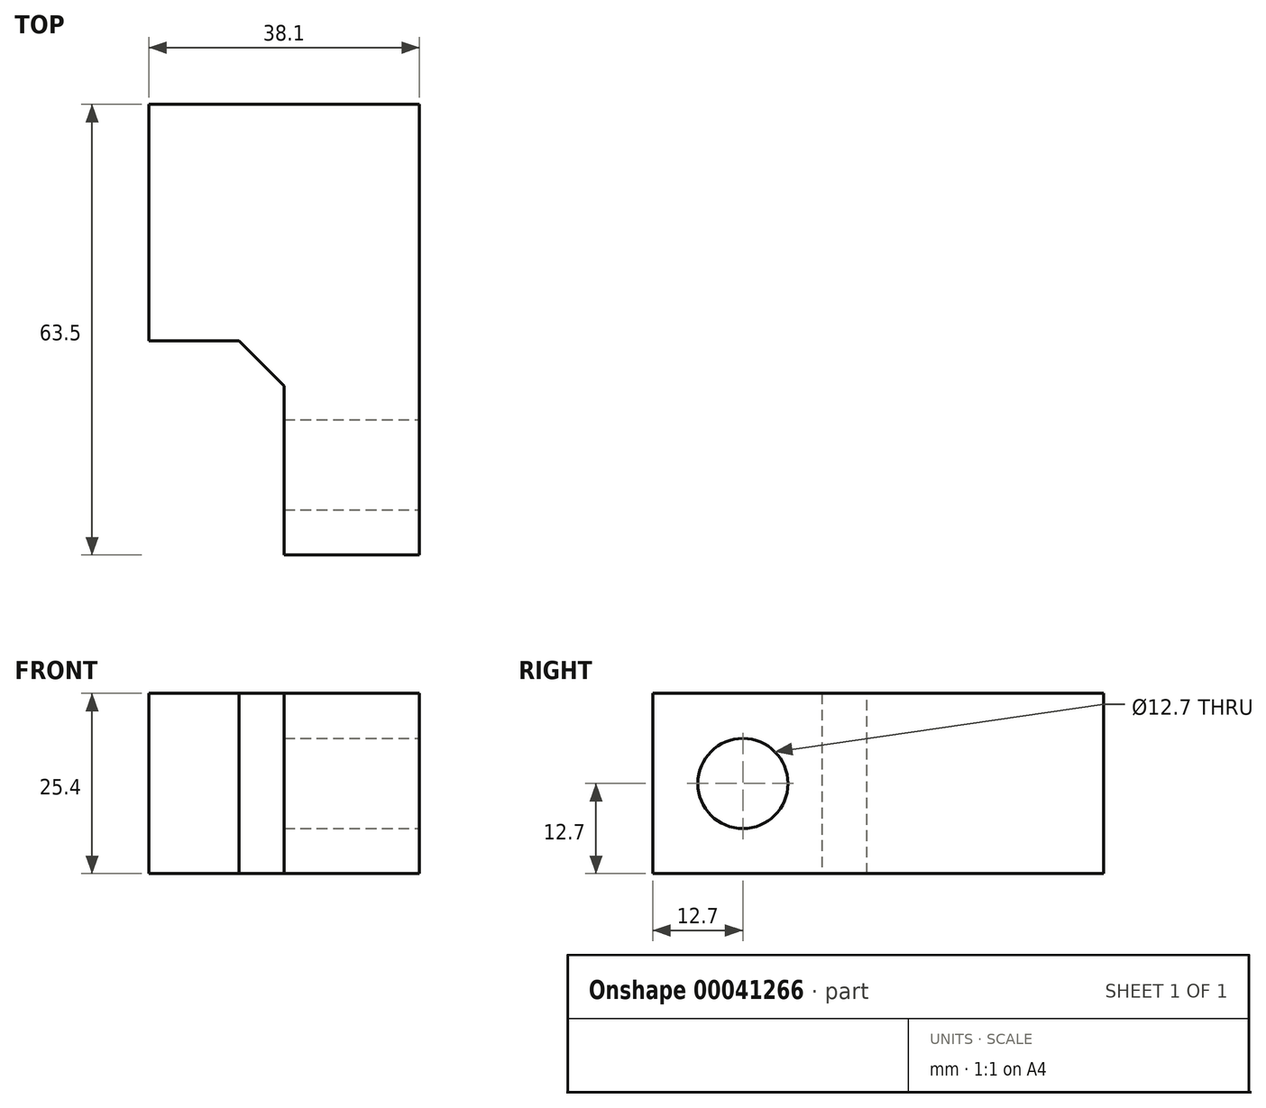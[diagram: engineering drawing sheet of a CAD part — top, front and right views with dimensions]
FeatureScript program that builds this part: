
annotation { "Feature Type Name" : "Feature", "Feature Type Description" : "" }
export const myFeature = defineFeature(function(context is Context, id is Id, definition is map)
    precondition{}
    {
        {
            var Q0;
            Q0=qCreatedBy(makeId("Top.planeOp"),FACE);
            var sketch = newSketch(context, id + "F0", { "sketchPlane" : qUnion([Q0])});
            skLineSegment(sketch, "E0.rect.bottom", {"start": v(-19.05, 31.75) * mm, "end": v(19.05, 31.75) * mm});
            skLineSegment(sketch, "E0.rect.top", {"start": v(-19.05, -31.75) * mm, "end": v(19.05, -31.75) * mm});
            skLineSegment(sketch, "E0.rect.left", {"start": v(-19.05, 31.75) * mm, "end": v(-19.05, -31.75) * mm});
            skLineSegment(sketch, "E0.rect.right", {"start": v(19.05, 31.75) * mm, "end": v(19.05, -31.75) * mm});
            skPoint(sketch, "E0.rect.middle", {"position": v(0, 0) * mm});
            skSolve(sketch);
        }
        {
            var Q0;
            Q0=makeQuery(id+"F0.imprint","IMPRINT",FACE,{"disambiguationData":[TD([[makeQuery(id+"F0.imprint","IMPRINT",EDGE,{"derivedFrom":sQuery(id+"F0.wireOp",EDGE,"E0.rect.bottom")}),-1.0]])]});
            extrude(context, id + "F1", {"entities" : qUnion([Q0]), "depth" : 25.4 * mm});
        }
        {
            var Q0;
            Q0=makeQuery(id+"F1.opExtrude","CAP_FACE",FACE,{"disambiguationData":[OSD([sQuery(id+"F0.wireOp",EDGE,"E0.rect.bottom"),sQuery(id+"F0.wireOp",EDGE,"E0.rect.top"),sQuery(id+"F0.wireOp",EDGE,"E0.rect.left"),sQuery(id+"F0.wireOp",EDGE,"E0.rect.right")])],"isStart":false});
            var sketch = newSketch(context, id + "F2", { "sketchPlane" : qUnion([Q0])});
            skLineSegment(sketch, "E1.bottom", {"start": v(-19.05, -31.75) * mm, "end": v(0, -31.75) * mm});
            skLineSegment(sketch, "E1.top", {"start": v(-19.05, -4.76) * mm, "end": v(0, -4.76) * mm});
            skLineSegment(sketch, "E1.left", {"start": v(-19.05, -31.75) * mm, "end": v(-19.05, -4.76) * mm});
            skLineSegment(sketch, "E1.right", {"start": v(0, -31.75) * mm, "end": v(0, -4.76) * mm});
            skSolve(sketch);
        }
        {
            var Q0;
            Q0=makeQuery(id+"F2.imprint","IMPRINT",FACE,{"disambiguationData":[TD([[makeQuery(id+"F2.imprint","IMPRINT",EDGE,{"derivedFrom":sQuery(id+"F2.wireOp",EDGE,"E1.bottom")}),1.0]])]});
            extrude(context, id + "F3", {"entities" : qUnion([Q0]), "operationType" : NewBodyOperationType.REMOVE, "oppositeDirection" : true, "depth" : 25.4 * mm});
        }
        {
            var Q0;
            Q0=makeQuery(id+"F1.opExtrude","SWEPT_FACE",FACE,{"disambiguationData":[OSD([sQuery(id+"F0.wireOp",EDGE,"E0.rect.right")])]});
            var sketch = newSketch(context, id + "F4", { "sketchPlane" : qUnion([Q0])});
            skCircle(sketch, "E2", {"center": v(-19.05, 12.7) * mm, "radius": 6.35 * mm});
            skSolve(sketch);
        }
        {
            var Q0;
            Q0=makeQuery(id+"F4.imprint","IMPRINT",FACE,{"disambiguationData":[TD([[makeQuery(id+"F4.imprint","IMPRINT",EDGE,{"derivedFrom":sQuery(id+"F4.wireOp",EDGE,"E2")}),1.0]])]});
            extrude(context, id + "F5", {"entities" : qUnion([Q0]), "operationType" : NewBodyOperationType.REMOVE, "oppositeDirection" : true, "depth" : 25.4 * mm});
        }
        {
            var Q0;
            Q0=makeQuery(id+"F3.boolean.opBoolean","COPY",FACE,{"derivedFrom":makeQuery(id+"F3.opExtrude","SWEPT_FACE",FACE,{"disambiguationData":[OSD([sQuery(id+"F2.wireOp",EDGE,"E1.top")])]})});
            extrude(context, id + "F6", {"entities" : qUnion([Q0]), "operationType" : NewBodyOperationType.REMOVE, "oppositeDirection" : true, "depth" : 3.17 * mm});
        }
        {
            var Q0;
            {var subQ0=sQuery(id+"F2.wireOp",EDGE,"E1.top");Q0=makeQuery(id+"F6.boolean.opBoolean","COPY",EDGE,{"derivedFrom":makeQuery(id+"F6.opExtrude","CAP_EDGE",EDGE,{"disambiguationData":[OSD([subQ0]),TDD([makeQuery(id+"F3.boolean.opBoolean","COPY",EDGE,{"derivedFrom":makeQuery(id+"F3.opExtrude","CAP_EDGE",EDGE,{"disambiguationData":[OSD([subQ0])],"isStart":true})})])],"isStart":false})});}
            var Q1;
            {var subQ0=sQuery(id+"F2.wireOp",EDGE,"E1.top");Q1=makeQuery(id+"F6.boolean.opBoolean","COPY",EDGE,{"derivedFrom":makeQuery(id+"F6.opExtrude","CAP_EDGE",EDGE,{"disambiguationData":[OSD([subQ0]),TDD([makeQuery(id+"F3.boolean.opBoolean","COPY",EDGE,{"derivedFrom":makeQuery(id+"F3.opExtrude","CAP_EDGE",EDGE,{"disambiguationData":[OSD([subQ0])],"isStart":false})})])],"isStart":false})});}
            chamfer(context, id + "F7", {"entities" : qUnion([Q0, Q1]), "width" : 6.35 * mm, "tangentPropagation" : true});
        }
    });
